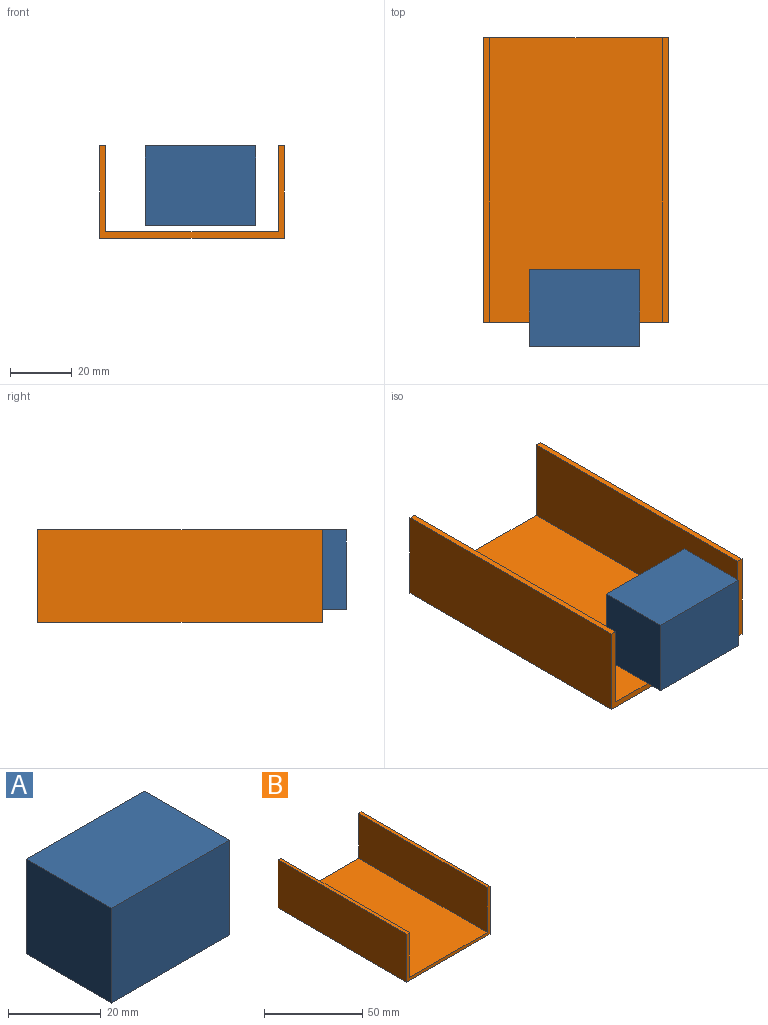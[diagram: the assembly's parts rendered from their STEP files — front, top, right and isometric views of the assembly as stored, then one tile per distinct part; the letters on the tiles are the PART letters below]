
ASSEMBLY  parts=2 mates=1
PART A: 6 faces, bbox 36x26x25 mm
  f0: plane 26x25mm, normal (-1,0,0), area 650mm2, adj f1,f3,f4,f5
  f1: plane 36x25mm, normal (0,-1,0), area 900mm2, adj f0,f2,f4,f5
  f2: plane 26x25mm, normal (1,0,0), area 650mm2, adj f1,f3,f4,f5
  f3: plane 36x25mm, normal (0,1,0), area 900mm2, adj f0,f2,f4,f5
  f4: plane 36x26mm, normal (0,0,-1), area 936mm2, adj f0,f1,f2,f3
  f5: plane 36x26mm, normal (0,0,1), area 936mm2, adj f0,f1,f2,f3
PART B: 10 faces, bbox 60x92.6x30 mm
  f0: plane 92.63x2mm, normal (0,0,1), area 185.3mm2, adj f1,f7,f8,f9
  f1: plane 92.63x30mm, normal (-1,0,0), area 2778.8mm2, adj f0,f2,f8,f9
  f2: plane 92.63x60mm, normal (0,0,-1), area 5557.6mm2, adj f1,f3,f8,f9
  f3: plane 92.63x30mm, normal (1,0,0), area 2778.8mm2, adj f2,f4,f8,f9
  f4: plane 92.63x2mm, normal (0,0,1), area 185.3mm2, adj f3,f5,f8,f9
  f5: plane 92.63x28mm, normal (-1,0,0), area 2593.6mm2, adj f4,f6,f8,f9
  f6: plane 92.63x56mm, normal (0,0,1), area 5187.1mm2, adj f5,f7,f8,f9
  f7: plane 92.63x28mm, normal (1,0,0), area 2593.6mm2, adj f0,f6,f8,f9
  f8: plane 60x30mm, normal (0,1,0), area 232mm2, adj f0,f1,f2,f3,f4,f5,f6,f7
  f9: plane 60x30mm, normal (0,-1,0), area 232mm2, adj f0,f1,f2,f3,f4,f5,f6,f7
PLACE A rot(axis=(1,0,0),90deg) t=(20.88,31.46,-18.48)mm
PLACE B t=(-14.93,-22.2,21.3)mm
MATE planar A.f3 <-> B.f0  axis (0,0,1) through (17.84,-17.5,21.3)mm
